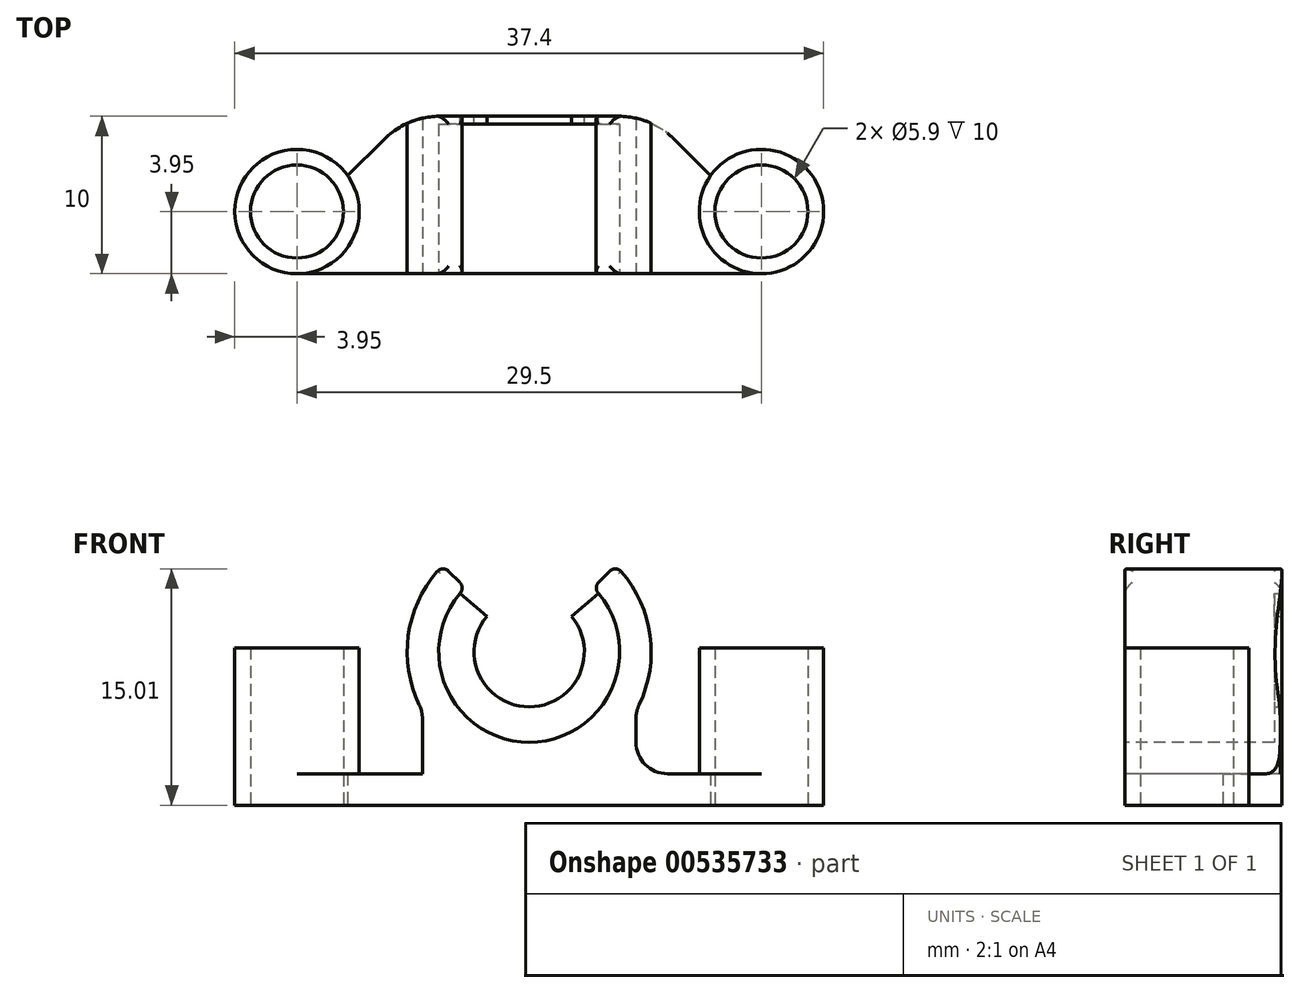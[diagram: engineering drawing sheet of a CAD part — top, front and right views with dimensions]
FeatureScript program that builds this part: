
annotation { "Feature Type Name" : "Feature", "Feature Type Description" : "" }
export const myFeature = defineFeature(function(context is Context, id is Id, definition is map)
    precondition{}
    {
        {
            var Q0;
            Q0=qCreatedBy(makeId("Top.planeOp"),FACE);
            var sketch = newSketch(context, id + "F0", { "sketchPlane" : qUnion([Q0])});
            skCircle(sketch, "E0", {"center": v(0, 0) * mm, "radius": 2.45 * mm});
            skCircle(sketch, "E1", {"center": v(29.5, 0) * mm, "radius": 2.45 * mm});
            skCircle(sketch, "E2.0", {"center": v(0, 0) * mm, "radius": 3.95 * mm});
            skCircle(sketch, "E3.0", {"center": v(29.5, 0) * mm, "radius": 3.95 * mm});
            skLineSegment(sketch, "E4", {"start": v(0, -3.95) * mm, "end": v(29.5, -3.95) * mm});
            skLineSegment(sketch, "E5", {"start": v(3.23, 2.28) * mm, "end": v(7, 6.05) * mm});
            skLineSegment(sketch, "E6", {"start": v(7, 6.05) * mm, "end": v(22.5, 6.05) * mm});
            skLineSegment(sketch, "E7", {"start": v(22.5, 6.05) * mm, "end": v(26.27, 2.28) * mm});
            skSolve(sketch);
        }
        {
            var Q0;
            {var subQ1=sQuery(id+"F0.wireOp",EDGE,"E4");Q0=makeQuery(id+"F0.imprint","IMPRINT",FACE,{"disambiguationData":[TD([[makeQuery(id+"F0.imprint","IMPRINT",EDGE,{"derivedFrom":subQ1}),1.0]])]});}
            var Q1;
            Q1=makeQuery(id+"F0.imprint","IMPRINT",FACE,{"disambiguationData":[TD([[makeQuery(id+"F0.imprint","IMPRINT",EDGE,{"derivedFrom":sQuery(id+"F0.wireOp",EDGE,"E0")}),-1.0]])]});
            var Q2;
            Q2=makeQuery(id+"F0.imprint","IMPRINT",FACE,{"disambiguationData":[TD([[makeQuery(id+"F0.imprint","IMPRINT",EDGE,{"derivedFrom":sQuery(id+"F0.wireOp",EDGE,"E0")}),1.0]])]});
            var Q3;
            Q3=makeQuery(id+"F0.imprint","IMPRINT",FACE,{"disambiguationData":[TD([[makeQuery(id+"F0.imprint","IMPRINT",EDGE,{"derivedFrom":sQuery(id+"F0.wireOp",EDGE,"E1")}),-1.0]])]});
            var Q4;
            Q4=makeQuery(id+"F0.imprint","IMPRINT",FACE,{"disambiguationData":[TD([[makeQuery(id+"F0.imprint","IMPRINT",EDGE,{"derivedFrom":sQuery(id+"F0.wireOp",EDGE,"E1")}),1.0]])]});
            extrude(context, id + "F1", {"entities" : qUnion([Q0, Q1, Q2, Q3, Q4]), "depth" : 2 * mm, "offsetDistance" : 25 * mm});
        }
        {
            var Q0;
            Q0=makeQuery(id+"F1.opExtrude","SWEPT_FACE",FACE,{"disambiguationData":[OSD([sQuery(id+"F0.wireOp",EDGE,"E4")])]});
            var sketch = newSketch(context, id + "F2", { "sketchPlane" : qUnion([Q0])});
            skLineSegment(sketch, "E8.0.0", {"start": v(0, 0) * mm, "end": v(29.5, 0) * mm});
            skLineSegment(sketch, "E8.0.1", {"start": v(29.5, 0) * mm, "end": v(29.5, 2) * mm});
            skLineSegment(sketch, "E8.0.2", {"start": v(29.5, 2) * mm, "end": v(0, 2) * mm});
            skLineSegment(sketch, "E8.0.3", {"start": v(0, 2) * mm, "end": v(0, 0) * mm});
            skArc(sketch, "E9", {"start": v(9.27, 15.23) * mm, "mid": v(14.75, 2) * mm, "end": v(20.23, 15.23) * mm});
            skPoint(sketch, "E9.centerSnap0", {"position": v(14.75, 2) * mm});
            skArc(sketch, "E10", {"start": v(10.68, 13.82) * mm, "mid": v(14.75, 4) * mm, "end": v(18.82, 13.82) * mm});
            skLineSegment(sketch, "E11", {"start": v(14.75, 9.75) * mm, "end": v(9.27, 15.23) * mm});
            skLineSegment(sketch, "E12", {"start": v(14.75, 9.75) * mm, "end": v(20.23, 15.23) * mm});
            skLineSegment(sketch, "E13", {"start": v(7.97, 6) * mm, "end": v(7.97, 2) * mm});
            skLineSegment(sketch, "E14", {"start": v(21.53, 6) * mm, "end": v(21.53, 2) * mm});
            skSolve(sketch);
        }
        {
            var Q0;
            {var subQ3=sQuery(id+"F2.wireOp",EDGE,"E10");Q0=makeQuery(id+"F2.imprint","IMPRINT",FACE,{"disambiguationData":[TD([[makeQuery(id+"F2.imprint","IMPRINT",EDGE,{"derivedFrom":subQ3}),-1.0]])]});}
            var Q1;
            {var subQ0=sQuery(id+"F2.wireOp",EDGE,"E13");Q1=makeQuery(id+"F2.imprint","IMPRINT",FACE,{"disambiguationData":[TD([[makeQuery(id+"F2.imprint","IMPRINT",EDGE,{"derivedFrom":subQ0}),1.0]])]});}
            var Q2;
            {var subQ0=sQuery(id+"F2.wireOp",EDGE,"E14");Q2=makeQuery(id+"F2.imprint","IMPRINT",FACE,{"disambiguationData":[TD([[makeQuery(id+"F2.imprint","IMPRINT",EDGE,{"derivedFrom":subQ0}),-1.0]])]});}
            var Q3;
            Q3=makeQuery(id+"F1.opExtrude","SWEPT_FACE",FACE,{"disambiguationData":[OSD([sQuery(id+"F0.wireOp",EDGE,"E6")])]});
            extrude(context, id + "F3", {"entities" : qUnion([Q0, Q1, Q2]), "operationType" : NewBodyOperationType.ADD, "endBound" : BoundingType.UP_TO_SURFACE, "oppositeDirection" : true, "depth" : 25 * mm, "endBoundEntityFace" : qUnion([Q3]), "offsetDistance" : 25 * mm});
        }
        {
            var Q0;
            Q0=makeQuery(id+"F3.opExtrude","SWEPT_FACE",FACE,{"disambiguationData":[OSD([sQuery(id+"F2.wireOp",EDGE,"E11")])]});
            var Q1;
            Q1=makeQuery(id+"F3.opExtrude","SWEPT_FACE",FACE,{"disambiguationData":[OSD([sQuery(id+"F2.wireOp",EDGE,"E12")])]});
            fillet(context, id + "F4", {"entities" : qUnion([Q0, Q1]), "radius" : .5 * mm, "tangentPropagation" : true, "allowEdgeOverflow" : false});
        }
        {
            var Q0;
            Q0=makeQuery(id+"F3.boolean.opBoolean","MERGE",FACE,{"derivedFrom":[makeQuery(id+"F1.opExtrude","SWEPT_FACE",FACE,{"disambiguationData":[OSD([sQuery(id+"F0.wireOp",EDGE,"E6")])]}),makeQuery(id+"F3.opExtrude","CAP_FACE",FACE,{"disambiguationData":[OSD([sQuery(id+"F2.wireOp",EDGE,"E8.0.2"),sQuery(id+"F2.wireOp",EDGE,"E9"),sQuery(id+"F2.wireOp",EDGE,"E10"),sQuery(id+"F2.wireOp",EDGE,"E11"),sQuery(id+"F2.wireOp",EDGE,"E12"),sQuery(id+"F2.wireOp",EDGE,"E13"),sQuery(id+"F2.wireOp",EDGE,"E14")])],"isStart":false})]});
            var sketch = newSketch(context, id + "F5", { "sketchPlane" : qUnion([Q0])});
            skArc(sketch, "E15.0.0", {"start": v(-8.9, 14.84) * mm, "mid": v(-8.92, 14.85) * mm, "end": v(-8.93, 14.86) * mm});
            skLineSegment(sketch, "E15.0.1", {"start": v(-8.93, 14.86) * mm, "end": v(-10.35, 13.45) * mm});
            skArc(sketch, "E15.0.2", {"start": v(-10.35, 13.45) * mm, "mid": v(-14.75, 4) * mm, "end": v(-19.15, 13.45) * mm});
            skLineSegment(sketch, "E15.0.3", {"start": v(-19.15, 13.45) * mm, "end": v(-20.57, 14.86) * mm});
            skArc(sketch, "E15.0.4", {"start": v(-20.57, 14.86) * mm, "mid": v(-20.58, 14.85) * mm, "end": v(-20.6, 14.84) * mm});
            skArc(sketch, "E15.0.5", {"start": v(-21.53, 6) * mm, "mid": v(-22.46, 10.57) * mm, "end": v(-20.6, 14.84) * mm});
            skLineSegment(sketch, "E15.0.6", {"start": v(-21.53, 6) * mm, "end": v(-21.53, 2) * mm});
            skLineSegment(sketch, "E15.0.7", {"start": v(-21.53, 2) * mm, "end": v(-22.5, 2) * mm});
            skLineSegment(sketch, "E15.0.8", {"start": v(-22.5, 2) * mm, "end": v(-22.5, 0) * mm});
            skLineSegment(sketch, "E15.0.9", {"start": v(-22.5, 0) * mm, "end": v(-7, 0) * mm});
            skLineSegment(sketch, "E15.0.10", {"start": v(-7, 0) * mm, "end": v(-7, 2) * mm});
            skLineSegment(sketch, "E15.0.11", {"start": v(-7, 2) * mm, "end": v(-7.97, 2) * mm});
            skLineSegment(sketch, "E15.0.12", {"start": v(-7.97, 2) * mm, "end": v(-7.97, 6) * mm});
            skArc(sketch, "E15.0.13", {"start": v(-8.9, 14.84) * mm, "mid": v(-7.04, 10.57) * mm, "end": v(-7.97, 6) * mm});
            skCircle(sketch, "E16", {"center": v(-14.75, 9.75) * mm, "radius": 3.5 * mm});
            skLineSegment(sketch, "E17", {"start": v(-14.75, 9.75) * mm, "end": v(-19.15, 13.45) * mm});
            skLineSegment(sketch, "E18", {"start": v(-14.75, 9.75) * mm, "end": v(-10.35, 13.45) * mm});
            skSolve(sketch);
        }
        {
            var Q0;
            {var subQ0=sQuery(id+"F5.wireOp",EDGE,"E15.0.2");Q0=makeQuery(id+"F5.imprint","IMPRINT",FACE,{"disambiguationData":[TD([[makeQuery(id+"F5.imprint","IMPRINT",EDGE,{"derivedFrom":subQ0}),-1.0]])]});}
            extrude(context, id + "F6", {"entities" : qUnion([Q0]), "operationType" : NewBodyOperationType.ADD, "oppositeDirection" : true, "depth" : .5 * mm, "offsetDistance" : 25 * mm});
        }
        {
            var Q0;
            {var subQ0=sQuery(id+"F0.wireOp",EDGE,"E6");var subQ1=sQuery(id+"F0.wireOp",EDGE,"E4");var subQ2=sQuery(id+"F0.wireOp",EDGE,"E5");var subQ3=sQuery(id+"F0.wireOp",EDGE,"E2.0");Q0=makeQuery(id+"F3.boolean.opBoolean","SPLIT",FACE,{"disambiguationData":[TD([makeQuery(id+"F1.opExtrude","SWEPT_FACE",FACE,{"disambiguationData":[OSD([subQ3])]})])],"derivedFrom":makeQuery(id+"F1.opExtrude","CAP_FACE",FACE,{"disambiguationData":[OSD([subQ3,sQuery(id+"F0.wireOp",EDGE,"E3.0"),subQ1,subQ2,subQ0,sQuery(id+"F0.wireOp",EDGE,"E7")])],"isStart":false})});}
            var sketch = newSketch(context, id + "F7", { "sketchPlane" : qUnion([Q0])});
            skCircle(sketch, "E19.0", {"center": v(0, 0) * mm, "radius": 3.95 * mm});
            skCircle(sketch, "E20.0", {"center": v(29.5, 0) * mm, "radius": 3.95 * mm});
            skSolve(sketch);
        }
        {
            var Q0;
            {var subQ0=sQuery(id+"F7.wireOp",EDGE,"E19.0");var subQ2=sQuery(id+"F0.wireOp",EDGE,"E5");var subQ6=makeQuery(id+"F7.imprint","INTERSECT",VERTEX,{"derivedFrom":[makeQuery(id+"F1.opExtrude","CAP_EDGE",EDGE,{"disambiguationData":[OSD([subQ2])],"isStart":false}),subQ0]});Q0=makeQuery(id+"F7.imprint","IMPRINT",FACE,{"disambiguationData":[TD([[makeQuery(id+"F7.imprint","IMPRINT",EDGE,{"disambiguationData":[TD([[subQ6,-1.0]])],"derivedFrom":subQ0}),1.0]])]});}
            var Q1;
            Q1=makeQuery(id+"F7.imprint","IMPRINT",FACE,{"disambiguationData":[TD([[makeQuery(id+"F7.imprint","IMPRINT",EDGE,{"derivedFrom":sQuery(id+"F7.wireOp",EDGE,"E20.0")}),1.0]])]});
            extrude(context, id + "F8", {"entities" : qUnion([Q0, Q1]), "operationType" : NewBodyOperationType.ADD, "depth" : 8 * mm, "offsetDistance" : 25 * mm});
        }
        {
            var Q0;
            Q0=makeQuery(id+"F0.imprint","IMPRINT",FACE,{"disambiguationData":[TD([[makeQuery(id+"F0.imprint","IMPRINT",EDGE,{"derivedFrom":sQuery(id+"F0.wireOp",EDGE,"E0")}),1.0]])]});
            var sketch = newSketch(context, id + "F9", { "sketchPlane" : qUnion([Q0])});
            skCircle(sketch, "E21.0.0", {"center": v(0, 0) * mm, "radius": 2.45 * mm});
            skCircle(sketch, "E22.0.0", {"center": v(29.5, 0) * mm, "radius": 2.45 * mm});
            skCircle(sketch, "E23.0", {"center": v(0, 0) * mm, "radius": 2.95 * mm});
            skCircle(sketch, "E24.0", {"center": v(29.5, 0) * mm, "radius": 2.95 * mm});
            skSolve(sketch);
        }
        {
            var Q0;
            Q0 = qSketchRegion(id + "F9", true);
            var Q1;
            Q1=makeQuery(id+"F9.imprint","IMPRINT",FACE,{"disambiguationData":[TD([[makeQuery(id+"F9.imprint","IMPRINT",EDGE,{"derivedFrom":sQuery(id+"F9.wireOp",EDGE,"E21.0.0")}),1.0]])]});
            var Q2;
            Q2=makeQuery(id+"F9.imprint","IMPRINT",FACE,{"disambiguationData":[TD([[makeQuery(id+"F9.imprint","IMPRINT",EDGE,{"derivedFrom":sQuery(id+"F9.wireOp",EDGE,"E22.0.0")}),1.0]])]});
            var Q3;
            Q3=makeQuery(id+"F8.opExtrude","CAP_FACE",FACE,{"disambiguationData":[OSD([sQuery(id+"F7.wireOp",EDGE,"E19.0")])],"isStart":false});
            extrude(context, id + "F10", {"entities" : qUnion([Q0, Q1, Q2]), "operationType" : NewBodyOperationType.REMOVE, "endBound" : BoundingType.UP_TO_SURFACE, "depth" : 25 * mm, "endBoundEntityFace" : qUnion([Q3]), "offsetDistance" : 25 * mm});
        }
        {
            var Q0;
            Q0=makeQuery(id+"F1.opExtrude","SWEPT_EDGE",EDGE,{"disambiguationData":[OSD([sQuery(id+"F0.wireOp",EDGE,"E5"),sQuery(id+"F0.wireOp",EDGE,"E6")])]});
            var Q1;
            Q1=makeQuery(id+"F1.opExtrude","SWEPT_EDGE",EDGE,{"disambiguationData":[OSD([sQuery(id+"F0.wireOp",EDGE,"E6"),sQuery(id+"F0.wireOp",EDGE,"E7")])]});
            fillet(context, id + "F11", {"entities" : qUnion([Q0, Q1]), "radius" : 5 * mm, "tangentPropagation" : true, "allowEdgeOverflow" : false});
        }
        {
            var Q0;
            Q0=makeQuery(id+"F8.opExtrude","CAP_EDGE",EDGE,{"disambiguationData":[OSD([sQuery(id+"F7.wireOp",EDGE,"E19.0")])],"isStart":true});
            var Q1;
            Q1=makeQuery(id+"F8.opExtrude","CAP_EDGE",EDGE,{"disambiguationData":[OSD([sQuery(id+"F7.wireOp",EDGE,"E20.0")])],"isStart":true});
            var Q2;
            Q2=makeQuery(id+"F3.opExtrude","SWEPT_EDGE",EDGE,{"disambiguationData":[OSD([sQuery(id+"F2.wireOp",EDGE,"E8.0.2"),sQuery(id+"F2.wireOp",EDGE,"E14")])]});
            var Q3;
            Q3=makeQuery(id+"F3.opExtrude","SWEPT_EDGE",EDGE,{"disambiguationData":[OSD([sQuery(id+"F2.wireOp",EDGE,"E8.0.2"),sQuery(id+"F2.wireOp",EDGE,"E13")])]});
            var Q4;
            Q4=makeQuery(id+"F3.opExtrude","SWEPT_EDGE",EDGE,{"disambiguationData":[OSD([sQuery(id+"F2.wireOp",EDGE,"E9"),sQuery(id+"F2.wireOp",EDGE,"E13")])]});
            var Q5;
            Q5=makeQuery(id+"F3.opExtrude","SWEPT_EDGE",EDGE,{"disambiguationData":[OSD([sQuery(id+"F2.wireOp",EDGE,"E9"),sQuery(id+"F2.wireOp",EDGE,"E14")])]});
            fillet(context, id + "F12", {"entities" : qUnion([Q0, Q1, Q2, Q3, Q4, Q5]), "radius" : 2 * mm, "tangentPropagation" : true, "allowEdgeOverflow" : false});
        }
    });
